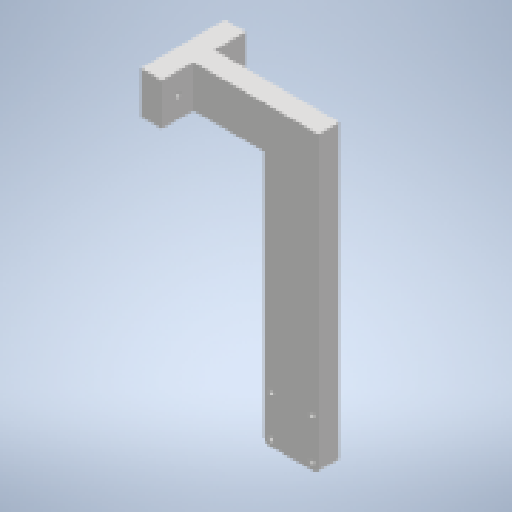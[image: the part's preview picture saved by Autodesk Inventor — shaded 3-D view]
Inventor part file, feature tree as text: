
AUTODESK INVENTOR PART (.ipt)
format: ipt  version: 2023.2 (Build 272271030, 271C)  size: 180,736 bytes
history: native  units: mm
features: reference x8, other x5, sheet_metal_op x3, sketch x2
ambient origin geometry x8: Origin, YZ Plane, XZ Plane, XY Plane, X Axis, Y Axis, Z Axis, Center Point
bodies: Solid1 (feature_tree)
feature tree (18):
  sheet_metal_op  "Face1"
  sheet_metal_op  "Face2"
  sketch  "Sketch1"  dims[d0=350.0mm]
  reference  "Reference1"
  reference  "Reference2"
  reference  "Reference3"
  reference  "Reference4"
  reference  "Reference5"
  reference  "Reference6"
  reference  "Reference7"
  reference  "Reference8"
  other  "Plate1"
  sketch  "Sketch2"  dims[d1=300.0mm d2=5.0mm d3=25.0mm d4=50.0mm d5=50.0mm d6=25.0mm d7=20.0mm d8=20.0mm d9=6.0mm d10=25.0mm d11=25.0mm d12=12.5mm d13=50.0mm d14=25.0mm]
  other  "Plate2"
  sheet_metal_op  "Bend1"
  other  "ensamble_general.iam"
  other  "patas:3"
  other  "lamina:1"
